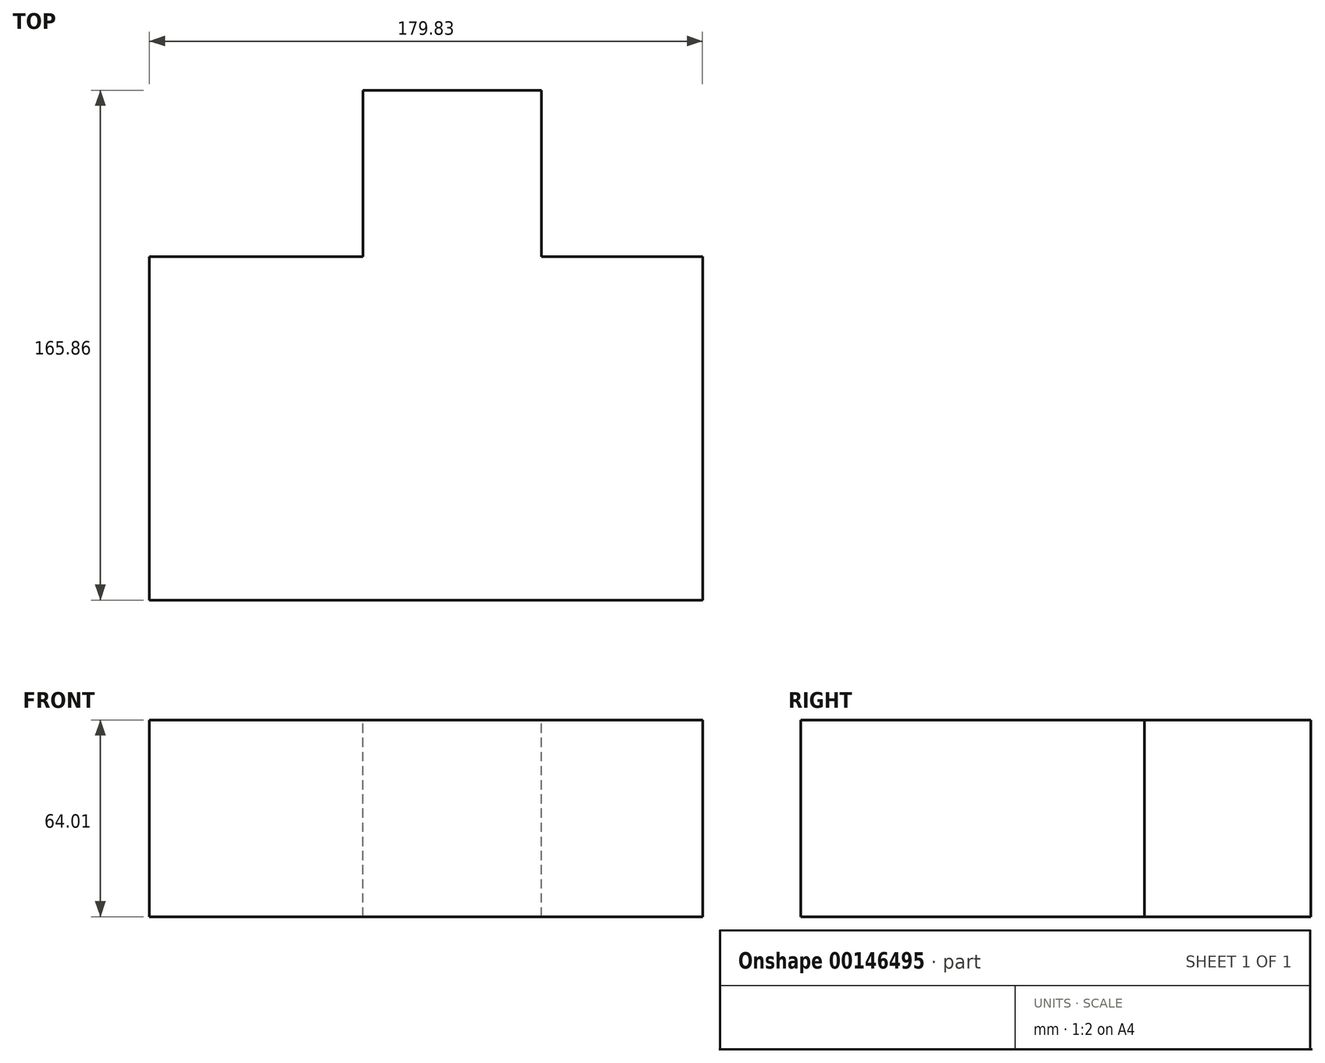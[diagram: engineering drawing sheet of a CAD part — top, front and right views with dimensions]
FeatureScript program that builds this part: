
annotation { "Feature Type Name" : "Feature", "Feature Type Description" : "" }
export const myFeature = defineFeature(function(context is Context, id is Id, definition is map)
    precondition{}
    {
        {
            var Q0;
            Q0=qCreatedBy(makeId("Top.planeOp"),FACE);
            var sketch = newSketch(context, id + "F0", { "sketchPlane" : qUnion([Q0])});
            skLineSegment(sketch, "E0", {"start": v(-22.57, 29.47) * mm, "end": v(-91.9, 29.47) * mm});
            skLineSegment(sketch, "E1", {"start": v(-91.9, 29.47) * mm, "end": v(-91.9, -82.3) * mm});
            skLineSegment(sketch, "E2", {"start": v(-91.9, -82.3) * mm, "end": v(87.92, -82.3) * mm});
            skLineSegment(sketch, "E3", {"start": v(87.92, -82.3) * mm, "end": v(87.92, 29.47) * mm});
            skLineSegment(sketch, "E4", {"start": v(87.92, 29.47) * mm, "end": v(35.6, 29.47) * mm});
            skLineSegment(sketch, "E5", {"start": v(-22.57, 29.47) * mm, "end": v(-22.57, 83.57) * mm});
            skLineSegment(sketch, "E6", {"start": v(-22.57, 83.57) * mm, "end": v(35.6, 83.57) * mm});
            skLineSegment(sketch, "E7", {"start": v(35.6, 83.57) * mm, "end": v(35.6, 29.47) * mm});
            skSolve(sketch);
        }
        {
            var Q0;
            Q0=sQuery(id+"F0.wireOp",EDGE,"E2");
            var Q1;
            Q1=sQuery(id+"F0.wireOp",EDGE,"E3");
            var Q2;
            Q2=sQuery(id+"F0.wireOp",EDGE,"E4");
            var Q3;
            Q3=sQuery(id+"F0.wireOp",EDGE,"E7");
            var Q4;
            Q4=sQuery(id+"F0.wireOp",EDGE,"E6");
            var Q5;
            Q5=sQuery(id+"F0.wireOp",EDGE,"E5");
            var Q6;
            Q6=sQuery(id+"F0.wireOp",EDGE,"E0");
            var Q7;
            Q7=sQuery(id+"F0.wireOp",EDGE,"E1");
            extrude(context, id + "F1", {"bodyType" : ToolBodyType.SURFACE, "surfaceEntities" : qUnion([Q0, Q1, Q2, Q3, Q4, Q5, Q6, Q7]), "depth" : 64 * mm});
        }
    });
